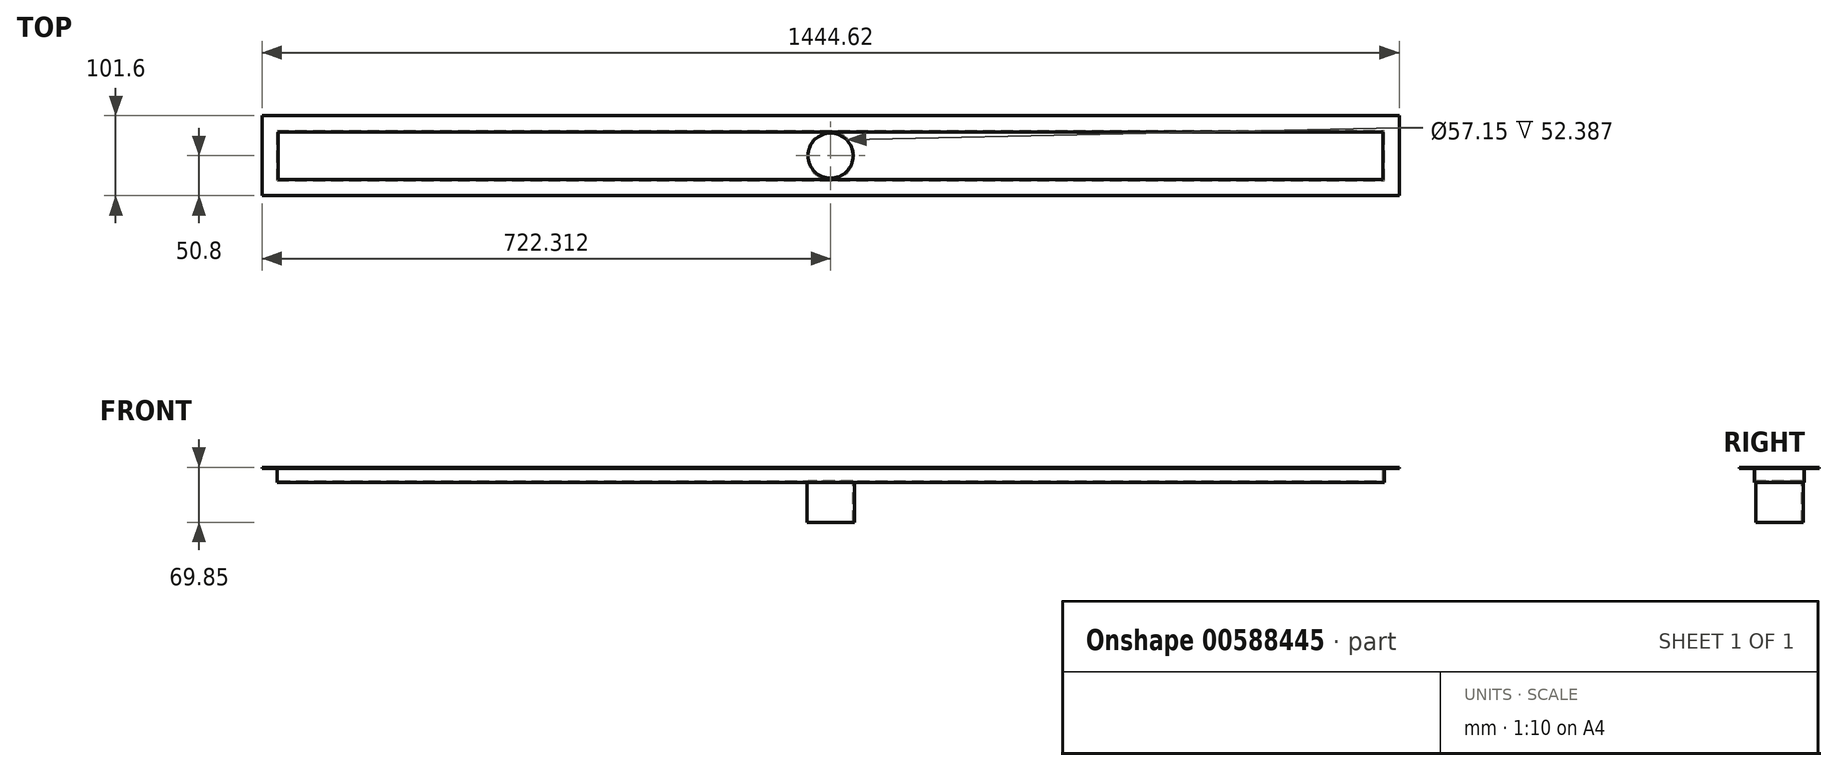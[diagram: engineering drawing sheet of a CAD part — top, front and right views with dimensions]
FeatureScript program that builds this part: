
annotation { "Feature Type Name" : "Feature", "Feature Type Description" : "" }
export const myFeature = defineFeature(function(context is Context, id is Id, definition is map)
    precondition{}
    {
        {
            var Q0;
            Q0=qCreatedBy(makeId("Top.planeOp"),FACE);
            var sketch = newSketch(context, id + "F0", { "sketchPlane" : qUnion([Q0])});
            skLineSegment(sketch, "E0.bottom", {"start": v(0, 0) * mm, "end": v(1444.62, 0) * mm});
            skLineSegment(sketch, "E0.top", {"start": v(0, 101.6) * mm, "end": v(1444.62, 101.6) * mm});
            skLineSegment(sketch, "E0.left", {"start": v(0, 0) * mm, "end": v(0, 101.6) * mm});
            skLineSegment(sketch, "E0.right", {"start": v(1444.62, 0) * mm, "end": v(1444.62, 101.6) * mm});
            skLineSegment(sketch, "E1.0", {"start": v(19.05, 19.05) * mm, "end": v(1425.58, 19.05) * mm});
            skLineSegment(sketch, "E1.1", {"start": v(19.05, 19.05) * mm, "end": v(19.05, 82.55) * mm});
            skLineSegment(sketch, "E1.2", {"start": v(19.05, 82.55) * mm, "end": v(1425.58, 82.55) * mm});
            skLineSegment(sketch, "E1.3", {"start": v(1425.58, 19.05) * mm, "end": v(1425.58, 82.55) * mm});
            skPoint(sketch, "E2", {"position": v(722.31, 82.55) * mm});
            skPoint(sketch, "E3", {"position": v(722.31, 19.05) * mm});
            skLineSegment(sketch, "E4", {"start": v(722.31, 82.55) * mm, "end": v(722.31, 19.05) * mm, "construction": true});
            skPoint(sketch, "E5", {"position": v(722.31, 50.8) * mm});
            skCircle(sketch, "E6", {"center": v(722.31, 50.8) * mm, "radius": 30.16 * mm});
            skCircle(sketch, "E7.0", {"center": v(722.31, 50.8) * mm, "radius": 28.58 * mm});
            skLineSegment(sketch, "E8.0", {"start": v(20.64, 80.96) * mm, "end": v(1423.99, 80.96) * mm});
            skLineSegment(sketch, "E8.1", {"start": v(20.64, 20.64) * mm, "end": v(20.64, 80.96) * mm});
            skLineSegment(sketch, "E8.2", {"start": v(20.64, 20.64) * mm, "end": v(1423.99, 20.64) * mm});
            skLineSegment(sketch, "E8.3", {"start": v(1423.99, 20.64) * mm, "end": v(1423.99, 80.96) * mm});
            skSolve(sketch);
        }
        {
            var Q0;
            Q0=makeQuery(id+"F0.imprint","IMPRINT",FACE,{"disambiguationData":[TD([[makeQuery(id+"F0.imprint","IMPRINT",EDGE,{"derivedFrom":sQuery(id+"F0.wireOp",EDGE,"E1.0")}),1.0]])]});
            var Q1;
            Q1=makeQuery(id+"F0.imprint","IMPRINT",FACE,{"disambiguationData":[TD([[makeQuery(id+"F0.imprint","IMPRINT",EDGE,{"derivedFrom":sQuery(id+"F0.wireOp",EDGE,"E0.bottom")}),1.0]])]});
            extrude(context, id + "F1", {"entities" : qUnion([Q0, Q1]), "oppositeDirection" : true, "depth" : 1.59 * mm, "offsetDistance" : 25.4 * mm});
        }
        {
            var Q0;
            Q0=makeQuery(id+"F0.imprint","IMPRINT",FACE,{"disambiguationData":[TD([[makeQuery(id+"F0.imprint","IMPRINT",EDGE,{"derivedFrom":sQuery(id+"F0.wireOp",EDGE,"E1.0")}),1.0]])]});
            var Q1;
            {var subQ5=sQuery(id+"F0.wireOp",EDGE,"E8.1");Q1=makeQuery(id+"F0.imprint","IMPRINT",FACE,{"disambiguationData":[TD([[makeQuery(id+"F0.imprint","IMPRINT",EDGE,{"derivedFrom":subQ5}),-1.0]])]});}
            var Q2;
            {var subQ5=sQuery(id+"F0.wireOp",EDGE,"E8.3");Q2=makeQuery(id+"F0.imprint","IMPRINT",FACE,{"disambiguationData":[TD([[makeQuery(id+"F0.imprint","IMPRINT",EDGE,{"derivedFrom":subQ5}),1.0]])]});}
            var Q3;
            Q3=makeQuery(id+"F0.imprint","IMPRINT",FACE,{"disambiguationData":[TD([[makeQuery(id+"F0.imprint","IMPRINT",EDGE,{"derivedFrom":sQuery(id+"F0.wireOp",EDGE,"E7.0")}),-1.0]])]});
            var Q4;
            Q4=makeQuery(id+"F0.imprint","IMPRINT",FACE,{"disambiguationData":[TD([[makeQuery(id+"F0.imprint","IMPRINT",EDGE,{"derivedFrom":sQuery(id+"F0.wireOp",EDGE,"E7.0")}),1.0]])]});
            extrude(context, id + "F2", {"entities" : qUnion([Q0, Q1, Q2, Q3, Q4]), "operationType" : NewBodyOperationType.ADD, "oppositeDirection" : true, "depth" : 19.05 * mm, "offsetDistance" : 25.4 * mm});
        }
        {
            var Q0;
            Q0=makeQuery(id+"F0.imprint","IMPRINT",FACE,{"disambiguationData":[TD([[makeQuery(id+"F0.imprint","IMPRINT",EDGE,{"derivedFrom":sQuery(id+"F0.wireOp",EDGE,"E7.0")}),-1.0]])]});
            extrude(context, id + "F3", {"entities" : qUnion([Q0]), "operationType" : NewBodyOperationType.ADD, "oppositeDirection" : true, "depth" : 69.85 * mm, "offsetDistance" : 25.4 * mm});
        }
        {
            var Q0;
            {var subQ5=sQuery(id+"F0.wireOp",EDGE,"E8.1");Q0=makeQuery(id+"F0.imprint","IMPRINT",FACE,{"disambiguationData":[TD([[makeQuery(id+"F0.imprint","IMPRINT",EDGE,{"derivedFrom":subQ5}),-1.0]])]});}
            var Q1;
            {var subQ5=sQuery(id+"F0.wireOp",EDGE,"E8.3");Q1=makeQuery(id+"F0.imprint","IMPRINT",FACE,{"disambiguationData":[TD([[makeQuery(id+"F0.imprint","IMPRINT",EDGE,{"derivedFrom":subQ5}),1.0]])]});}
            var Q2;
            Q2=makeQuery(id+"F0.imprint","IMPRINT",FACE,{"disambiguationData":[TD([[makeQuery(id+"F0.imprint","IMPRINT",EDGE,{"derivedFrom":sQuery(id+"F0.wireOp",EDGE,"E7.0")}),-1.0]])]});
            var Q3;
            Q3=makeQuery(id+"F0.imprint","IMPRINT",FACE,{"disambiguationData":[TD([[makeQuery(id+"F0.imprint","IMPRINT",EDGE,{"derivedFrom":sQuery(id+"F0.wireOp",EDGE,"E7.0")}),1.0]])]});
            extrude(context, id + "F4", {"entities" : qUnion([Q0, Q1, Q2, Q3]), "operationType" : NewBodyOperationType.REMOVE, "oppositeDirection" : true, "depth" : 17.46 * mm, "offsetDistance" : 25.4 * mm});
        }
        {
            var Q0;
            Q0=makeQuery(id+"F0.imprint","IMPRINT",FACE,{"disambiguationData":[TD([[makeQuery(id+"F0.imprint","IMPRINT",EDGE,{"derivedFrom":sQuery(id+"F0.wireOp",EDGE,"E7.0")}),1.0]])]});
            extrude(context, id + "F5", {"entities" : qUnion([Q0]), "operationType" : NewBodyOperationType.REMOVE, "endBound" : BoundingType.THROUGH_ALL, "oppositeDirection" : true, "depth" : 25.4 * mm, "offsetDistance" : 25.4 * mm});
        }
    });
